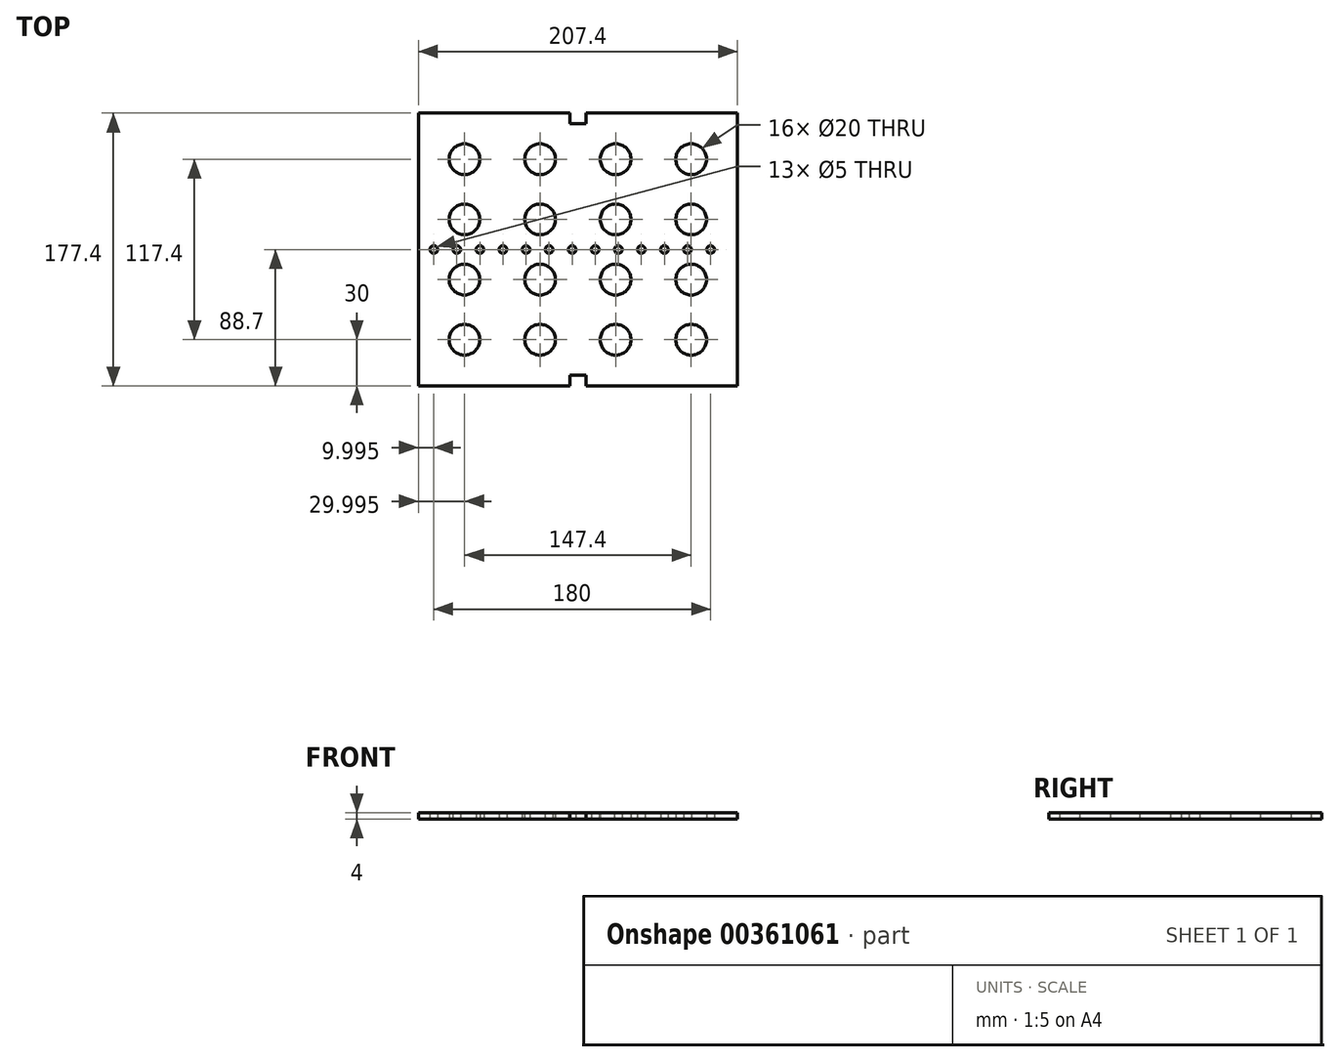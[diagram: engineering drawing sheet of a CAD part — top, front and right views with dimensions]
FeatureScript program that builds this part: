
annotation { "Feature Type Name" : "Feature", "Feature Type Description" : "" }
export const myFeature = defineFeature(function(context is Context, id is Id, definition is map)
    precondition{}
    {
        {
            var Q0;
            Q0=qCreatedBy(makeId("Top.planeOp"),FACE);
            var sketch = newSketch(context, id + "F0", { "sketchPlane" : qUnion([Q0])});
            skLineSegment(sketch, "E0.bottom", {"start": v(-96.5, 143.82) * mm, "end": v(1.96, 143.82) * mm});
            skLineSegment(sketch, "E0.top", {"start": v(-96.5, -33.58) * mm, "end": v(1.96, -33.58) * mm});
            skLineSegment(sketch, "E0.left", {"start": v(-96.5, 143.82) * mm, "end": v(-96.5, -33.58) * mm});
            skLineSegment(sketch, "E0.right", {"start": v(110.9, 143.82) * mm, "end": v(110.9, -33.58) * mm});
            skPoint(sketch, "E1.centerSnap1", {"position": v(-96.5, 55.12) * mm});
            skCircle(sketch, "E2", {"center": v(80.9, 113.82) * mm, "radius": 10 * mm});
            skCircle(sketch, "E3.0.1.0", {"center": v(80.9, 74.69) * mm, "radius": 10 * mm});
            skCircle(sketch, "E3.0.2.0", {"center": v(80.9, 35.55) * mm, "radius": 10 * mm});
            skCircle(sketch, "E3.0.3.0", {"center": v(80.9, -3.58) * mm, "radius": 10 * mm});
            skCircle(sketch, "E3.1.0.0", {"center": v(31.77, 113.82) * mm, "radius": 10 * mm});
            skCircle(sketch, "E3.1.1.0", {"center": v(31.77, 74.69) * mm, "radius": 10 * mm});
            skCircle(sketch, "E3.1.2.0", {"center": v(31.77, 35.55) * mm, "radius": 10 * mm});
            skCircle(sketch, "E3.1.3.0", {"center": v(31.77, -3.58) * mm, "radius": 10 * mm});
            skCircle(sketch, "E3.2.0.0", {"center": v(-17.36, 113.82) * mm, "radius": 10 * mm});
            skCircle(sketch, "E3.2.1.0", {"center": v(-17.36, 74.69) * mm, "radius": 10 * mm});
            skCircle(sketch, "E3.2.2.0", {"center": v(-17.36, 35.55) * mm, "radius": 10 * mm});
            skCircle(sketch, "E3.2.3.0", {"center": v(-17.36, -3.58) * mm, "radius": 10 * mm});
            skCircle(sketch, "E3.3.0.0", {"center": v(-66.5, 113.82) * mm, "radius": 10 * mm});
            skCircle(sketch, "E3.3.1.0", {"center": v(-66.5, 74.69) * mm, "radius": 10 * mm});
            skCircle(sketch, "E3.3.2.0", {"center": v(-66.5, 35.55) * mm, "radius": 10 * mm});
            skCircle(sketch, "E3.3.3.0", {"center": v(-66.5, -3.58) * mm, "radius": 10 * mm});
            skLineSegment(sketch, "E3.direction1", {"start": v(80.9, 113.82) * mm, "end": v(31.77, 113.82) * mm, "construction": true});
            skLineSegment(sketch, "E3.direction2", {"start": v(80.9, 113.82) * mm, "end": v(80.9, 74.69) * mm, "construction": true});
            skLineSegment(sketch, "E4", {"start": v(-66.5, -33.58) * mm, "end": v(-96.5, -33.58) * mm, "construction": true});
            skLineSegment(sketch, "E5", {"start": v(-96.5, -33.58) * mm, "end": v(-96.5, -3.58) * mm, "construction": true});
            skLineSegment(sketch, "E6", {"start": v(-96.5, -3.58) * mm, "end": v(-66.5, -3.58) * mm, "construction": true});
            skLineSegment(sketch, "E7", {"start": v(-66.5, -3.58) * mm, "end": v(-66.5, -33.58) * mm, "construction": true});
            skLineSegment(sketch, "E8", {"start": v(-96.5, 55.12) * mm, "end": v(110.9, 55.12) * mm, "construction": true});
            skPoint(sketch, "E9", {"position": v(-86.5, 55.12) * mm});
            skPoint(sketch, "E10.1.0.0", {"position": v(-71.5, 55.12) * mm});
            skPoint(sketch, "E10.2.0.0", {"position": v(-56.5, 55.12) * mm});
            skPoint(sketch, "E10.3.0.0", {"position": v(-41.5, 55.12) * mm});
            skPoint(sketch, "E10.4.0.0", {"position": v(-26.5, 55.12) * mm});
            skPoint(sketch, "E10.5.0.0", {"position": v(-11.5, 55.12) * mm});
            skPoint(sketch, "E10.6.0.0", {"position": v(3.5, 55.12) * mm});
            skPoint(sketch, "E10.7.0.0", {"position": v(18.5, 55.12) * mm});
            skPoint(sketch, "E10.8.0.0", {"position": v(33.5, 55.12) * mm});
            skPoint(sketch, "E10.9.0.0", {"position": v(48.5, 55.12) * mm});
            skPoint(sketch, "E10.10.0.0", {"position": v(63.5, 55.12) * mm});
            skPoint(sketch, "E10.11.0.0", {"position": v(78.5, 55.12) * mm});
            skPoint(sketch, "E10.12.0.0", {"position": v(93.5, 55.12) * mm});
            skLineSegment(sketch, "E10.direction1", {"start": v(-86.5, 55.12) * mm, "end": v(-71.5, 55.12) * mm, "construction": true});
            skPoint(sketch, "E11", {"position": v(7.2, 143.82) * mm});
            skPoint(sketch, "E12", {"position": v(7.2, -33.58) * mm});
            skLineSegment(sketch, "E13", {"start": v(1.96, 143.82) * mm, "end": v(1.96, 136.82) * mm});
            skLineSegment(sketch, "E14", {"start": v(1.96, 136.82) * mm, "end": v(12.46, 136.82) * mm});
            skLineSegment(sketch, "E15", {"start": v(12.46, 136.82) * mm, "end": v(12.46, 143.82) * mm});
            skLineSegment(sketch, "E16.trimOffspring", {"start": v(12.46, 143.82) * mm, "end": v(110.9, 143.82) * mm});
            skLineSegment(sketch, "E17", {"start": v(1.96, -33.58) * mm, "end": v(1.96, -26.58) * mm});
            skLineSegment(sketch, "E18", {"start": v(1.96, -26.58) * mm, "end": v(12.46, -26.58) * mm});
            skLineSegment(sketch, "E19", {"start": v(12.46, -26.58) * mm, "end": v(12.46, -33.58) * mm});
            skLineSegment(sketch, "E20.trimOffspring", {"start": v(12.46, -33.58) * mm, "end": v(110.9, -33.58) * mm});
            skLineSegment(sketch, "E21", {"start": v(7.2, 143.82) * mm, "end": v(7.2, -33.58) * mm, "construction": true});
            skSolve(sketch);
        }
        {
            var Q0;
            Q0=makeQuery(id+"F0.imprint","IMPRINT",FACE,{"disambiguationData":[TD([[makeQuery(id+"F0.imprint","IMPRINT",EDGE,{"derivedFrom":sQuery(id+"F0.wireOp",EDGE,"E0.bottom")}),-1.0]])]});
            extrude(context, id + "F1", {"entities" : qUnion([Q0]), "depth" : 4 * mm});
        }
        {
            var Q0;
            Q0=sQuery(id+"F0.wireOp",VERTEX,"E10.7.0.0");
            var Q1;
            Q1=sQuery(id+"F0.wireOp",VERTEX,"E10.5.0.0");
            var Q2;
            Q2=sQuery(id+"F0.wireOp",VERTEX,"E10.2.0.0");
            var Q3;
            Q3=sQuery(id+"F0.wireOp",VERTEX,"E10.18.0.0");
            var Q4;
            Q4=sQuery(id+"F0.wireOp",VERTEX,"E10.14.0.0");
            var Q5;
            Q5=sQuery(id+"F0.wireOp",VERTEX,"E10.12.0.0");
            var Q6;
            Q6=sQuery(id+"F0.wireOp",VERTEX,"E10.4.0.0");
            var Q7;
            Q7=sQuery(id+"F0.wireOp",VERTEX,"E10.11.0.0");
            var Q8;
            Q8=sQuery(id+"F0.wireOp",VERTEX,"E10.10.0.0");
            var Q9;
            Q9=sQuery(id+"F0.wireOp",VERTEX,"E10.1.0.0");
            var Q10;
            Q10=sQuery(id+"F0.wireOp",VERTEX,"E10.17.0.0");
            var Q11;
            Q11=sQuery(id+"F0.wireOp",VERTEX,"E10.8.0.0");
            var Q12;
            Q12=sQuery(id+"F0.wireOp",VERTEX,"E10.3.0.0");
            var Q13;
            Q13=sQuery(id+"F0.wireOp",VERTEX,"E10.19.0.0");
            var Q14;
            Q14=sQuery(id+"F0.wireOp",VERTEX,"E10.15.0.0");
            var Q15;
            Q15=sQuery(id+"F0.wireOp",VERTEX,"E10.13.0.0");
            var Q16;
            Q16=sQuery(id+"F0.wireOp",VERTEX,"E10.6.0.0");
            var Q17;
            Q17=sQuery(id+"F0.wireOp",VERTEX,"E10.9.0.0");
            var Q18;
            Q18=sQuery(id+"F0.wireOp",VERTEX,"E9");
            var Q19;
            Q19=sQuery(id+"F0.wireOp",VERTEX,"E10.16.0.0");
            var Q20;
            Q20=makeQuery(id+"F1.opExtrude","SWEPT_BODY",BODY,{"disambiguationData":[OSD([sQuery(id+"F0.wireOp",EDGE,"E0.bottom"),sQuery(id+"F0.wireOp",EDGE,"E0.top"),sQuery(id+"F0.wireOp",EDGE,"E0.left"),sQuery(id+"F0.wireOp",EDGE,"E0.right"),sQuery(id+"F0.wireOp",EDGE,"E2"),sQuery(id+"F0.wireOp",EDGE,"E3.0.1.0"),sQuery(id+"F0.wireOp",EDGE,"E3.0.2.0"),sQuery(id+"F0.wireOp",EDGE,"E3.0.3.0"),sQuery(id+"F0.wireOp",EDGE,"E3.1.0.0"),sQuery(id+"F0.wireOp",EDGE,"E3.1.1.0"),sQuery(id+"F0.wireOp",EDGE,"E3.1.2.0"),sQuery(id+"F0.wireOp",EDGE,"E3.1.3.0"),sQuery(id+"F0.wireOp",EDGE,"E3.2.0.0"),sQuery(id+"F0.wireOp",EDGE,"E3.2.1.0"),sQuery(id+"F0.wireOp",EDGE,"E3.2.2.0"),sQuery(id+"F0.wireOp",EDGE,"E3.2.3.0"),sQuery(id+"F0.wireOp",EDGE,"E3.3.0.0"),sQuery(id+"F0.wireOp",EDGE,"E3.3.1.0"),sQuery(id+"F0.wireOp",EDGE,"E3.3.2.0"),sQuery(id+"F0.wireOp",EDGE,"E3.3.3.0")])]});
            hole(context, id + "F2", {"style" : HoleStyle.SIMPLE, "endStyle" : HoleEndStyle.THROUGH, "oppositeDirection" : true, "holeDiameter" : 5 * mm, "isTappedThrough" : true, "tappedDepth" : 12 * mm, "tapClearance" : 3, "locations" : qUnion([Q0, Q1, Q2, Q3, Q4, Q5, Q6, Q7, Q8, Q9, Q10, Q11, Q12, Q13, Q14, Q15, Q16, Q17, Q18, Q19]), "scope" : qUnion([Q20])});
        }
        {
            var Q0;
            Q0=makeQuery(id+"F1.opExtrude","SWEPT_FACE",FACE,{"disambiguationData":[OSD([sQuery(id+"F0.wireOp",EDGE,"E0.top")])]});
            var sketch = newSketch(context, id + "F3", { "sketchPlane" : qUnion([Q0])});
            skLineSegment(sketch, "E22", {"start": v(-96.5, 2) * mm, "end": v(-96.5, -28) * mm, "construction": true});
            skLineSegment(sketch, "E23", {"start": v(-96.5, 2) * mm, "end": v(-96.5, 32.07) * mm, "construction": true});
            skLineSegment(sketch, "E24", {"start": v(110.9, 2) * mm, "end": v(110.9, 32.09) * mm, "construction": true});
            skLineSegment(sketch, "E25", {"start": v(110.9, 2) * mm, "end": v(110.9, -28.9) * mm, "construction": true});
            skLineSegment(sketch, "E26", {"start": v(-96.5, 2) * mm, "end": v(110.9, 2) * mm, "construction": true});
            skPoint(sketch, "E27", {"position": v(7.2, 2) * mm});
            skLineSegment(sketch, "E28", {"start": v(7.2, 2) * mm, "end": v(12.46, 2) * mm});
            skLineSegment(sketch, "E29", {"start": v(12.46, 2) * mm, "end": v(12.46, 7) * mm});
            skLineSegment(sketch, "E30", {"start": v(7.2, 2) * mm, "end": v(1.96, 2) * mm});
            skLineSegment(sketch, "E31", {"start": v(1.96, 2) * mm, "end": v(1.96, -3) * mm});
            skSolve(sketch);
        }
        {
            var Q0;
            Q0=sQuery(id+"F3.wireOp",EDGE,"E31");
            var Q1;
            Q1=sQuery(id+"F3.wireOp",EDGE,"E30");
            var Q2;
            Q2=sQuery(id+"F3.wireOp",EDGE,"E28");
            var Q3;
            Q3=sQuery(id+"F3.wireOp",EDGE,"E29");
            extrude(context, id + "F4", {"bodyType" : ToolBodyType.SURFACE, "surfaceEntities" : qUnion([Q0, Q1, Q2, Q3]), "oppositeDirection" : true, "depth" : 202.5 * mm, "offsetDistance" : 25 * mm, "hasSecondDirection" : true, "secondDirectionOppositeDirection" : false, "secondDirectionDepth" : 32.3 * mm});
        }
    });
